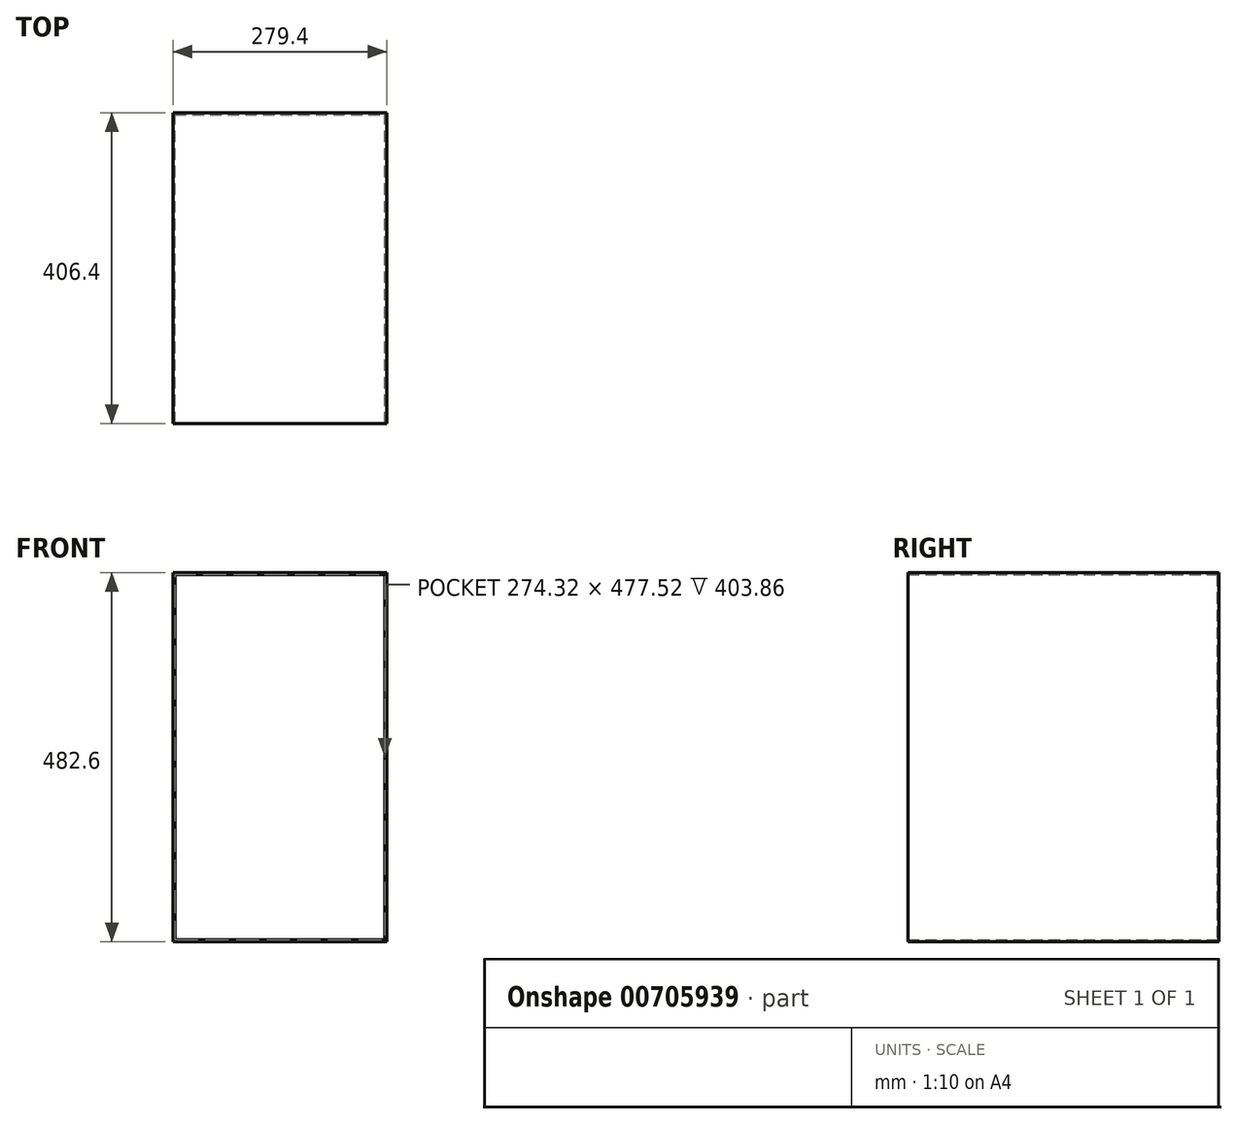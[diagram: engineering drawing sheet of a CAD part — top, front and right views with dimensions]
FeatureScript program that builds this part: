
annotation { "Feature Type Name" : "Feature", "Feature Type Description" : "" }
export const myFeature = defineFeature(function(context is Context, id is Id, definition is map)
    precondition{}
    {
        {
            var Q0;
            Q0=qCreatedBy(makeId("Front.planeOp"),FACE);
            var sketch = newSketch(context, id + "F0", { "sketchPlane" : qUnion([Q0])});
            skLineSegment(sketch, "E0.bottom", {"start": v(-255.8, 282.47) * mm, "end": v(23.6, 282.47) * mm});
            skLineSegment(sketch, "E0.top", {"start": v(-255.8, -200.13) * mm, "end": v(23.6, -200.13) * mm});
            skLineSegment(sketch, "E0.left", {"start": v(-255.8, 282.47) * mm, "end": v(-255.8, -200.13) * mm});
            skLineSegment(sketch, "E0.right", {"start": v(23.6, 282.47) * mm, "end": v(23.6, -200.13) * mm});
            skSolve(sketch);
        }
        {
            var Q0;
            Q0=makeQuery(id+"F0.imprint","IMPRINT",FACE,{"disambiguationData":[TD([[makeQuery(id+"F0.imprint","IMPRINT",EDGE,{"derivedFrom":sQuery(id+"F0.wireOp",EDGE,"E0.bottom")}),-1.0]])]});
            extrude(context, id + "F1", {"entities" : qUnion([Q0]), "depth" : 25.4 * mm, "offsetDistance" : 25.4 * mm});
        }
        {
            var Q0;
            Q0=qCreatedBy(makeId("Front.planeOp"),FACE);
            var sketch = newSketch(context, id + "F2", { "sketchPlane" : qUnion([Q0])});
            skSolve(sketch);
        }
        {
            var Q0;
            Q0 = qSketchRegion(id + "F2", true);
            var Q1;
            Q1=makeQuery(id+"F1.opExtrude","CAP_FACE",FACE,{"disambiguationData":[OSD([sQuery(id+"F0.wireOp",EDGE,"E0.bottom"),sQuery(id+"F0.wireOp",EDGE,"E0.top"),sQuery(id+"F0.wireOp",EDGE,"E0.left"),sQuery(id+"F0.wireOp",EDGE,"E0.right")])],"isStart":false});
            extrude(context, id + "F3", {"entities" : qUnion([Q0, Q1]), "operationType" : NewBodyOperationType.ADD, "depth" : 381 * mm, "offsetDistance" : 25.4 * mm});
        }
        {
            var Q0;
            Q0=makeQuery(id+"F3.opExtrude","CAP_FACE",FACE,{"disambiguationData":[OSD([sQuery(id+"F0.wireOp",EDGE,"E0.bottom"),sQuery(id+"F0.wireOp",EDGE,"E0.top"),sQuery(id+"F0.wireOp",EDGE,"E0.left"),sQuery(id+"F0.wireOp",EDGE,"E0.right")])],"isStart":false});
            shell(context, id + "F4", {"entities" : qUnion([Q0]), "thickness" : 2.54 * mm});
        }
    });
